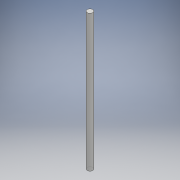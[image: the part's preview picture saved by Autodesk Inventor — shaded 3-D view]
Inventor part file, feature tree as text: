
AUTODESK INVENTOR PART (.ipt)
format: ipt  version: 2018 (Build 220112000, 112)  size: 90,624 bytes
history: native  units: mm
features: other x1, extrude x1, sketch x1
ambient origin geometry x8: Origin, YZ Plane, XZ Plane, XY Plane, X Axis, Y Axis, Z Axis, Center Point
bodies: Body1 (feature_tree)
feature tree (3):
  other  "ソリッド1"
  extrude  "押し出し1"  Depth=12.0mm
  sketch  "スケッチ1"
